# Revit family: PRD_FrankeWS_WtrArtrs_TapAerator_ZAQUA087
name_source: partatom
category: Generic Models
revit_build: Autodesk Revit 2018 (Build: 20190510_1515(x64)
units: mm (PartAtom-declared; Revit-internal decimal feet)

## family parameters
Always vertical = No
Can host rebar = No
Cut with Voids When Loaded = No
Part Type = Normal
Room Calculation Point = No
Round Connector Dimension = Use Diameter
Shared = No
Work Plane-Based = Yes

## types (1)
- ZAQUA087
    AssetType = Fixed
    BIMObjectName = PRD_AR_WtrArtrs_TapAerator_ZAQUA087
    Category = Pr_60_55_97_95, Water aerators
    Color = no colour
    Default Elevation = 1219 mm
    Description = Theft-proof aerator with integrated flow regulator 0.10 l/s, with male thread M 24 x 1.
    DurationUnit = year
    Features = Theft-proof water aerator ZAQUA087
    FillingQuantity = 1 piece
    GrossWeight = 0.03 kg
    IfcExportAs = IfcElementAssembly
    IfcExportType = USERDEFINED
    InstallationDate = 1900-12-31T23:59:59
    MainColor = stainless steel
    Manufacturer = KWC Group AG
    ManufacturerName = KWC Group AG
    ManufacturerURL = www.kwc.com
    Material = stainless steel
    Model = ZAQUA087
    ModelNumber = 2000101160
    ModelReference = ZAQUA087
    NBSDescription = Water aerators
    NBSReference = 90-15-90/335
    Name = Tap Aerator ZAQUA087
    NetWeight = 0.03 kg
    ProductInformation = https://pim.kwc.com
    URL = www.kwc.com
    Uniclass2015Code = Pr_60_55_97_95
    Uniclass2015Title = Water aerators
    Uniclass2015Version = Products v1.10
    Version = 1
    WarrantyDurationUnit = year
    WarrantyStartDate = 1900-12-31T23:59:59
